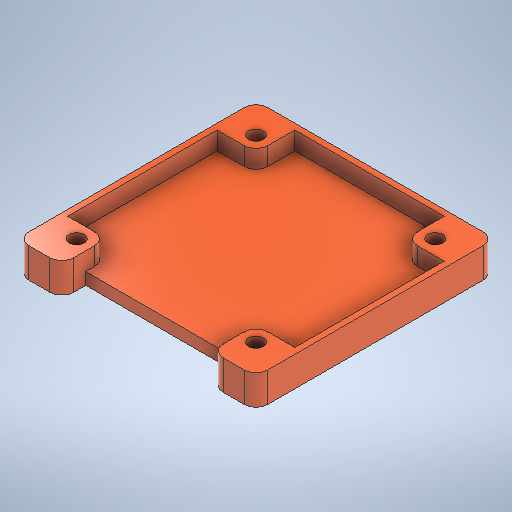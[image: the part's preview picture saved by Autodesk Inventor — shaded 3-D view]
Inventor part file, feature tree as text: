
AUTODESK INVENTOR PART (.ipt)
format: ipt  version: 2025 (Build 290162010, 162A)  size: 338,944 bytes
history: native  units: mm
features: extrude x3, sketch x3, fillet x1
ambient origin geometry x8: Origin, YZ Plane, XZ Plane, XY Plane, X Axis, Y Axis, Z Axis, Center Point
bodies: Solid1 (feature_tree)
feature tree (7):
  extrude  "Extrusion1"  Depth=38.0mm
  extrude  "Extrusion2"  Depth=2.5mm
  extrude  "Extrusion3"  Depth=2.0mm
  fillet  "Fillet1"  Radius=4.0mm
  sketch  "Sketch1"  dims[d0=38.0mm d1=38.0mm]
  sketch  "Sketch2"  dims[d2=2.5mm d3=2.5mm]
  sketch  "Sketch3"  dims[d4=2.5mm d5=2.5mm d6=4.0mm d7=4.0mm d8=4.0mm d9=4.0mm d10=40.0mm d11=40.0mm d12=5.0mm d13=0.0mm d14=25.0mm d15=6.5mm d16=25.0mm d17=7.5mm d18=6.5mm d19=6.5mm d20=25.0mm d21=6.5mm d22=12.5mm d24=12.5mm d25=3.0mm d26=0.0mm d27=4.0mm d28=3.0mm d29=0.0mm d30=2.0mm]
